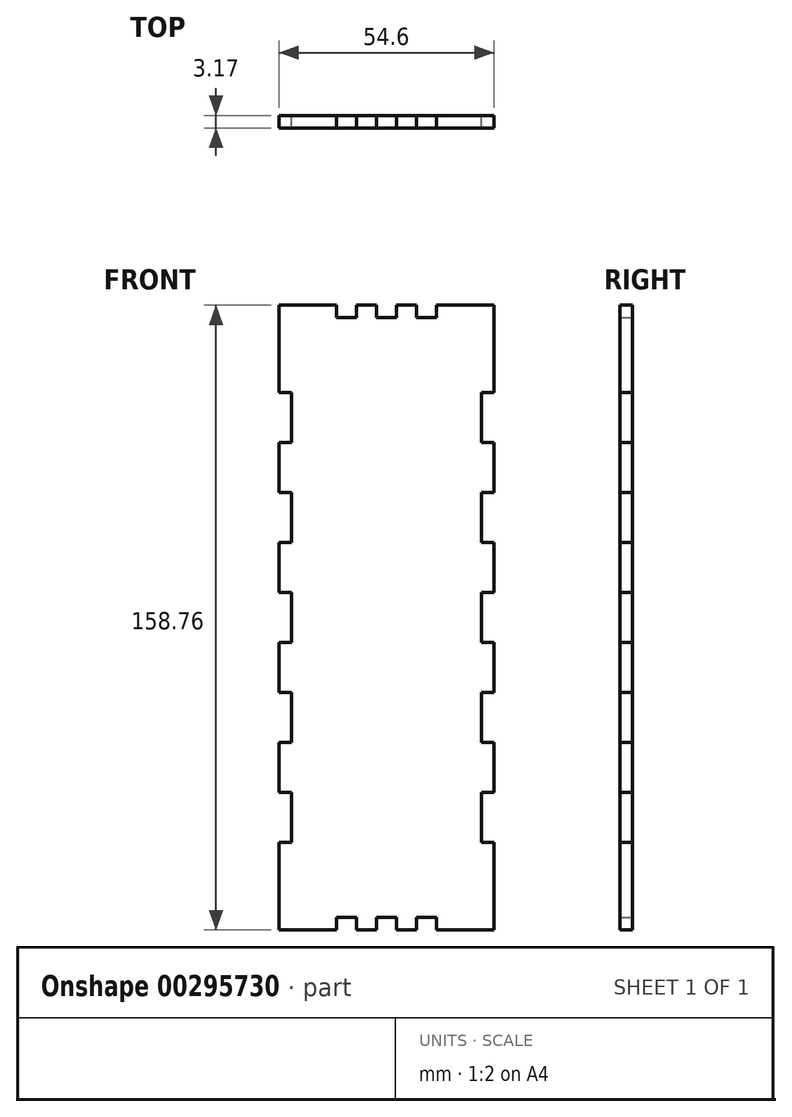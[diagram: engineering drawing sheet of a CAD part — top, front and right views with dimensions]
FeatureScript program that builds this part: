
annotation { "Feature Type Name" : "Feature", "Feature Type Description" : "" }
export const myFeature = defineFeature(function(context is Context, id is Id, definition is map)
    precondition{}
    {
        {
            var Q0;
            Q0=qCreatedBy(makeId("Front.planeOp"),FACE);
            var sketch = newSketch(context, id + "F0", { "sketchPlane" : qUnion([Q0])});
            skLineSegment(sketch, "E0.bottom", {"start": v(27.3, -79.38) * mm, "end": v(-27.3, -79.38) * mm, "construction": true});
            skLineSegment(sketch, "E0.top", {"start": v(27.3, 79.38) * mm, "end": v(-27.3, 79.38) * mm, "construction": true});
            skLineSegment(sketch, "E0.left", {"start": v(27.3, -79.38) * mm, "end": v(27.3, 79.38) * mm, "construction": true});
            skPoint(sketch, "E0.middle", {"position": v(0, 0) * mm});
            skLineSegment(sketch, "E1.bottom", {"start": v(24.13, -76.2) * mm, "end": v(-24.13, -76.2) * mm, "construction": true});
            skLineSegment(sketch, "E1.top", {"start": v(24.13, 76.2) * mm, "end": v(-24.13, 76.2) * mm, "construction": true});
            skLineSegment(sketch, "E1.left", {"start": v(24.13, -76.2) * mm, "end": v(24.13, 76.2) * mm, "construction": true});
            skLineSegment(sketch, "E1.right", {"start": v(-24.13, -76.2) * mm, "end": v(-24.13, 76.2) * mm, "construction": true});
            skLineSegment(sketch, "E2", {"start": v(-12.7, 79.38) * mm, "end": v(-27.3, 79.38) * mm});
            skLineSegment(sketch, "E3.MirrorCS", {"start": v(12.7, 79.38) * mm, "end": v(27.3, 79.38) * mm});
            skLineSegment(sketch, "E4.MirrorCS", {"start": v(-12.7, -79.38) * mm, "end": v(-27.3, -79.38) * mm});
            skLineSegment(sketch, "E5.MirrorCS", {"start": v(12.7, -79.38) * mm, "end": v(27.3, -79.38) * mm});
            skLineSegment(sketch, "E6.top", {"start": v(-12.7, -76.2) * mm, "end": v(-7.62, -76.2) * mm});
            skLineSegment(sketch, "E6.left", {"start": v(-12.7, -79.38) * mm, "end": v(-12.7, -76.2) * mm});
            skLineSegment(sketch, "E6.right", {"start": v(-7.62, -79.38) * mm, "end": v(-7.62, -76.2) * mm});
            skLineSegment(sketch, "E7.top", {"start": v(-7.62, -79.38) * mm, "end": v(-2.54, -79.38) * mm});
            skLineSegment(sketch, "E7.left", {"start": v(-7.62, -76.2) * mm, "end": v(-7.62, -79.38) * mm});
            skLineSegment(sketch, "E7.right", {"start": v(-2.54, -76.2) * mm, "end": v(-2.54, -79.38) * mm});
            skLineSegment(sketch, "E8.top", {"start": v(-2.54, -76.2) * mm, "end": v(2.54, -76.2) * mm});
            skLineSegment(sketch, "E8.left", {"start": v(-2.54, -79.38) * mm, "end": v(-2.54, -76.2) * mm});
            skLineSegment(sketch, "E8.right", {"start": v(2.54, -79.38) * mm, "end": v(2.54, -76.2) * mm});
            skLineSegment(sketch, "E9.top", {"start": v(2.54, -79.38) * mm, "end": v(7.62, -79.38) * mm});
            skLineSegment(sketch, "E9.left", {"start": v(2.54, -76.2) * mm, "end": v(2.54, -79.38) * mm});
            skLineSegment(sketch, "E9.right", {"start": v(7.62, -76.2) * mm, "end": v(7.62, -79.38) * mm});
            skLineSegment(sketch, "E10.top", {"start": v(12.7, -76.2) * mm, "end": v(7.62, -76.2) * mm});
            skLineSegment(sketch, "E10.left", {"start": v(12.7, -79.38) * mm, "end": v(12.7, -76.2) * mm});
            skLineSegment(sketch, "E10.right", {"start": v(7.62, -79.38) * mm, "end": v(7.62, -76.2) * mm});
            skLineSegment(sketch, "E11.MirrorCS", {"start": v(-12.7, 79.38) * mm, "end": v(-12.7, 76.2) * mm});
            skLineSegment(sketch, "E12.MirrorCS", {"start": v(-12.7, 76.2) * mm, "end": v(-7.62, 76.2) * mm});
            skLineSegment(sketch, "E13.MirrorCS", {"start": v(-7.62, 79.38) * mm, "end": v(-7.62, 76.2) * mm});
            skLineSegment(sketch, "E14.MirrorCS", {"start": v(-7.62, 79.38) * mm, "end": v(-2.54, 79.38) * mm});
            skLineSegment(sketch, "E15.MirrorCS", {"start": v(-2.54, 76.2) * mm, "end": v(-2.54, 79.38) * mm});
            skLineSegment(sketch, "E16.MirrorCS", {"start": v(-2.54, 76.2) * mm, "end": v(2.54, 76.2) * mm});
            skLineSegment(sketch, "E17.MirrorCS", {"start": v(2.54, 79.38) * mm, "end": v(2.54, 76.2) * mm});
            skLineSegment(sketch, "E18.MirrorCS", {"start": v(2.54, 79.38) * mm, "end": v(7.62, 79.38) * mm});
            skLineSegment(sketch, "E19.MirrorCS", {"start": v(7.62, 76.2) * mm, "end": v(7.62, 79.38) * mm});
            skLineSegment(sketch, "E20.MirrorCS", {"start": v(12.7, 76.2) * mm, "end": v(7.62, 76.2) * mm});
            skLineSegment(sketch, "E21.MirrorCS", {"start": v(12.7, 79.38) * mm, "end": v(12.7, 76.2) * mm});
            skLineSegment(sketch, "E22.bottom", {"start": v(24.13, -6.35) * mm, "end": v(27.3, -6.35) * mm});
            skLineSegment(sketch, "E22.top", {"start": v(24.13, 6.35) * mm, "end": v(27.3, 6.35) * mm});
            skLineSegment(sketch, "E22.left", {"start": v(24.13, -6.35) * mm, "end": v(24.13, 6.35) * mm});
            skLineSegment(sketch, "E23.bottom", {"start": v(27.3, 6.35) * mm, "end": v(24.13, 6.35) * mm});
            skLineSegment(sketch, "E23.top", {"start": v(27.3, 19.05) * mm, "end": v(24.13, 19.05) * mm});
            skLineSegment(sketch, "E23.left", {"start": v(27.3, 6.35) * mm, "end": v(27.3, 19.05) * mm});
            skLineSegment(sketch, "E24.bottom", {"start": v(24.13, 19.05) * mm, "end": v(27.3, 19.05) * mm});
            skLineSegment(sketch, "E24.top", {"start": v(24.13, 31.75) * mm, "end": v(27.3, 31.75) * mm});
            skLineSegment(sketch, "E24.left", {"start": v(24.13, 19.05) * mm, "end": v(24.13, 31.75) * mm});
            skLineSegment(sketch, "E25.bottom", {"start": v(27.3, 31.75) * mm, "end": v(24.13, 31.75) * mm});
            skLineSegment(sketch, "E25.top", {"start": v(27.3, 44.45) * mm, "end": v(24.13, 44.45) * mm});
            skLineSegment(sketch, "E25.left", {"start": v(27.3, 31.75) * mm, "end": v(27.3, 44.45) * mm});
            skLineSegment(sketch, "E26.bottom", {"start": v(24.13, 44.45) * mm, "end": v(27.3, 44.45) * mm});
            skLineSegment(sketch, "E26.top", {"start": v(24.13, 57.15) * mm, "end": v(27.3, 57.15) * mm});
            skLineSegment(sketch, "E26.left", {"start": v(24.13, 44.45) * mm, "end": v(24.13, 57.15) * mm});
            skLineSegment(sketch, "E27.MirrorCS", {"start": v(27.3, -19.05) * mm, "end": v(24.13, -19.05) * mm});
            skLineSegment(sketch, "E28.MirrorCS", {"start": v(24.13, -44.45) * mm, "end": v(27.3, -44.45) * mm});
            skLineSegment(sketch, "E29.MirrorCS", {"start": v(27.3, -31.75) * mm, "end": v(24.13, -31.75) * mm});
            skLineSegment(sketch, "E30.MirrorCS", {"start": v(27.3, -44.45) * mm, "end": v(24.13, -44.45) * mm});
            skLineSegment(sketch, "E31.MirrorCS", {"start": v(24.13, -31.75) * mm, "end": v(27.3, -31.75) * mm});
            skLineSegment(sketch, "E32.MirrorCS", {"start": v(24.13, -19.05) * mm, "end": v(27.3, -19.05) * mm});
            skLineSegment(sketch, "E33.MirrorCS", {"start": v(24.13, -57.15) * mm, "end": v(27.3, -57.15) * mm});
            skLineSegment(sketch, "E34.MirrorCS", {"start": v(24.13, -44.45) * mm, "end": v(24.13, -57.15) * mm});
            skLineSegment(sketch, "E35.MirrorCS", {"start": v(24.13, -19.05) * mm, "end": v(24.13, -31.75) * mm});
            skLineSegment(sketch, "E36.MirrorCS", {"start": v(27.3, -31.75) * mm, "end": v(27.3, -44.45) * mm});
            skLineSegment(sketch, "E37", {"start": v(27.3, -6.35) * mm, "end": v(27.3, -19.05) * mm});
            skLineSegment(sketch, "E38", {"start": v(27.3, 79.38) * mm, "end": v(27.3, 57.15) * mm});
            skLineSegment(sketch, "E39", {"start": v(27.3, -57.15) * mm, "end": v(27.3, -79.38) * mm});
            skLineSegment(sketch, "E40.MirrorCS", {"start": v(-27.3, 19.05) * mm, "end": v(-24.13, 19.05) * mm});
            skLineSegment(sketch, "E41.MirrorCS", {"start": v(-24.13, -19.05) * mm, "end": v(-27.3, -19.05) * mm});
            skLineSegment(sketch, "E42.MirrorCS", {"start": v(-27.3, -31.75) * mm, "end": v(-24.13, -31.75) * mm});
            skLineSegment(sketch, "E43.MirrorCS", {"start": v(-24.13, 6.35) * mm, "end": v(-27.3, 6.35) * mm});
            skLineSegment(sketch, "E44.MirrorCS", {"start": v(-27.3, 44.45) * mm, "end": v(-24.13, 44.45) * mm});
            skLineSegment(sketch, "E45.MirrorCS", {"start": v(-24.13, 31.75) * mm, "end": v(-27.3, 31.75) * mm});
            skLineSegment(sketch, "E46.MirrorCS", {"start": v(-27.3, -44.45) * mm, "end": v(-24.13, -44.45) * mm});
            skLineSegment(sketch, "E47.MirrorCS", {"start": v(-24.13, 44.45) * mm, "end": v(-27.3, 44.45) * mm});
            skLineSegment(sketch, "E48.MirrorCS", {"start": v(-27.3, 6.35) * mm, "end": v(-24.13, 6.35) * mm});
            skLineSegment(sketch, "E49.MirrorCS", {"start": v(-24.13, -44.45) * mm, "end": v(-27.3, -44.45) * mm});
            skLineSegment(sketch, "E50.MirrorCS", {"start": v(-27.3, 31.75) * mm, "end": v(-24.13, 31.75) * mm});
            skLineSegment(sketch, "E51.MirrorCS", {"start": v(-24.13, -31.75) * mm, "end": v(-27.3, -31.75) * mm});
            skLineSegment(sketch, "E52.MirrorCS", {"start": v(-27.3, -19.05) * mm, "end": v(-24.13, -19.05) * mm});
            skLineSegment(sketch, "E53.MirrorCS", {"start": v(-24.13, 19.05) * mm, "end": v(-27.3, 19.05) * mm});
            skLineSegment(sketch, "E54.MirrorCS", {"start": v(-24.13, -6.35) * mm, "end": v(-27.3, -6.35) * mm});
            skLineSegment(sketch, "E55.MirrorCS", {"start": v(-24.13, 57.15) * mm, "end": v(-27.3, 57.15) * mm});
            skLineSegment(sketch, "E56.MirrorCS", {"start": v(-24.13, -57.15) * mm, "end": v(-27.3, -57.15) * mm});
            skLineSegment(sketch, "E57.MirrorCS", {"start": v(-24.13, -6.35) * mm, "end": v(-24.13, 6.35) * mm});
            skLineSegment(sketch, "E58.MirrorCS", {"start": v(-27.3, -6.35) * mm, "end": v(-27.3, -19.05) * mm});
            skLineSegment(sketch, "E59.MirrorCS", {"start": v(-27.3, 31.75) * mm, "end": v(-27.3, 44.45) * mm});
            skLineSegment(sketch, "E60.MirrorCS", {"start": v(-27.3, -79.38) * mm, "end": v(-27.3, 79.38) * mm, "construction": true});
            skLineSegment(sketch, "E61.MirrorCS", {"start": v(-27.3, 79.38) * mm, "end": v(-27.3, 57.15) * mm});
            skLineSegment(sketch, "E62.MirrorCS", {"start": v(-24.13, 44.45) * mm, "end": v(-24.13, 57.15) * mm});
            skLineSegment(sketch, "E63.MirrorCS", {"start": v(-24.13, -19.05) * mm, "end": v(-24.13, -31.75) * mm});
            skLineSegment(sketch, "E64.MirrorCS", {"start": v(-24.13, 19.05) * mm, "end": v(-24.13, 31.75) * mm});
            skLineSegment(sketch, "E65.MirrorCS", {"start": v(-27.3, -57.15) * mm, "end": v(-27.3, -79.38) * mm});
            skLineSegment(sketch, "E66.MirrorCS", {"start": v(-27.3, 6.35) * mm, "end": v(-27.3, 19.05) * mm});
            skLineSegment(sketch, "E67.MirrorCS", {"start": v(-24.13, -44.45) * mm, "end": v(-24.13, -57.15) * mm});
            skLineSegment(sketch, "E68.MirrorCS", {"start": v(-27.3, -31.75) * mm, "end": v(-27.3, -44.45) * mm});
            skSolve(sketch);
        }
        {
            var Q0;
            Q0 = qSketchRegion(id + "F0", true);
            extrude(context, id + "F1", {"entities" : qUnion([Q0]), "depth" : 3.17 * mm});
        }
    });
